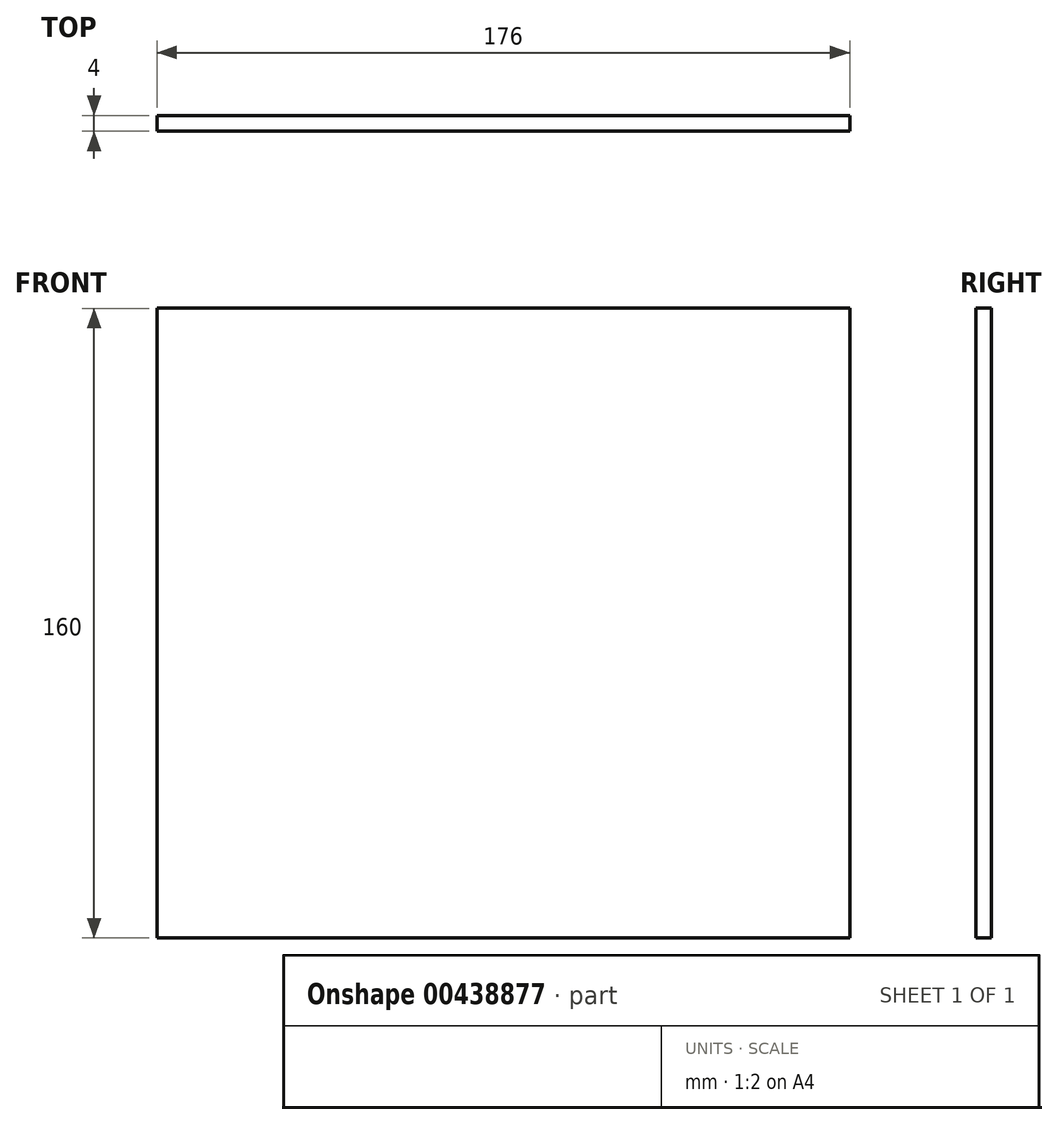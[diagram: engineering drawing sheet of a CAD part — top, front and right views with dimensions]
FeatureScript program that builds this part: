
annotation { "Feature Type Name" : "Feature", "Feature Type Description" : "" }
export const myFeature = defineFeature(function(context is Context, id is Id, definition is map)
    precondition{}
    {
        {
            var Q0;
            Q0=qCreatedBy(makeId("Front.planeOp"),FACE);
            var sketch = newSketch(context, id + "F0", { "sketchPlane" : qUnion([Q0])});
            skLineSegment(sketch, "E0", {"start": v(-89.15, 108.97) * mm, "end": v(86.85, 108.97) * mm});
            skLineSegment(sketch, "E1", {"start": v(86.85, 108.97) * mm, "end": v(86.85, -51.03) * mm});
            skLineSegment(sketch, "E2", {"start": v(86.85, -51.03) * mm, "end": v(-89.15, -51.03) * mm});
            skLineSegment(sketch, "E3", {"start": v(-89.15, -51.03) * mm, "end": v(-89.15, 108.97) * mm});
            skSolve(sketch);
        }
        {
            var Q0;
            Q0 = qSketchRegion(id + "F0", true);
            extrude(context, id + "F1", {"entities" : qUnion([Q0]), "depth" : 4 * mm});
        }
    });
